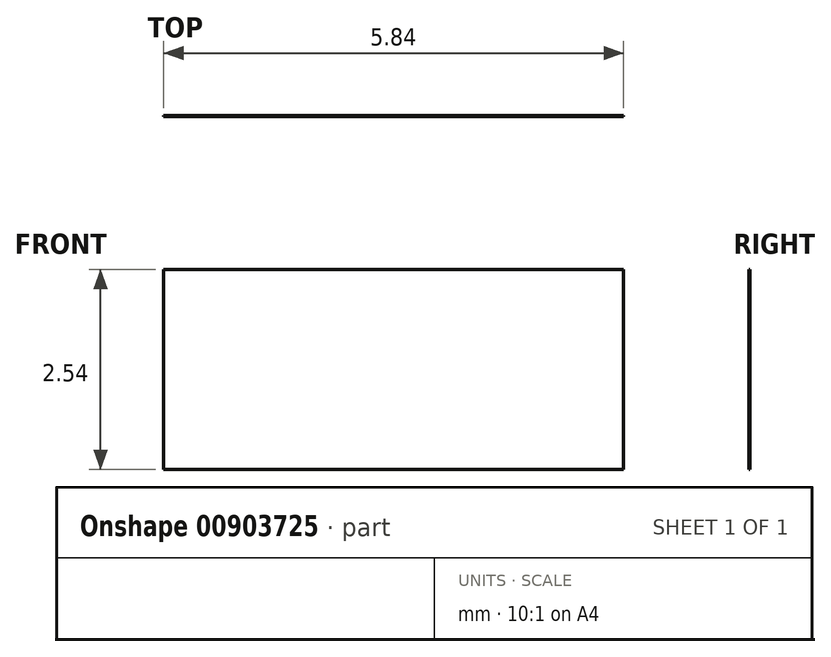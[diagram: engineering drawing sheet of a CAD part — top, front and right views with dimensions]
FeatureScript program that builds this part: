
annotation { "Feature Type Name" : "Feature", "Feature Type Description" : "" }
export const myFeature = defineFeature(function(context is Context, id is Id, definition is map)
    precondition{}
    {
        {
            var Q0;
            Q0=qCreatedBy(makeId("Front.planeOp"),FACE);
            var sketch = newSketch(context, id + "F0", { "sketchPlane" : qUnion([Q0])});
            skLineSegment(sketch, "E0", {"start": v(0, 0) * mm, "end": v(0, 12.7) * mm});
            skLineSegment(sketch, "E1", {"start": v(0, 12.7) * mm, "end": v(10.16, 12.7) * mm});
            skLineSegment(sketch, "E2", {"start": v(10.16, 12.7) * mm, "end": v(10.16, 10.16) * mm});
            skLineSegment(sketch, "E3", {"start": v(10.16, 10.16) * mm, "end": v(56.13, 10.16) * mm});
            skLineSegment(sketch, "E4", {"start": v(56.13, 10.16) * mm, "end": v(56.13, 12.7) * mm});
            skLineSegment(sketch, "E5", {"start": v(56.13, 12.7) * mm, "end": v(66.3, 12.7) * mm});
            skLineSegment(sketch, "E6", {"start": v(66.3, 12.7) * mm, "end": v(66.3, 0) * mm});
            skLineSegment(sketch, "E7", {"start": v(66.3, 0) * mm, "end": v(0, 0) * mm});
            skLineSegment(sketch, "E8", {"start": v(5.84, 15.24) * mm, "end": v(-0.5, 15.24) * mm});
            skLineSegment(sketch, "E9", {"start": v(-0.5, 15.24) * mm, "end": v(-10.88, 3.85) * mm});
            skLineSegment(sketch, "E10", {"start": v(0, 0) * mm, "end": v(-6.65, 0) * mm});
            skCircle(sketch, "E11", {"center": v(-6.65, 0) * mm, "radius": 5.72 * mm});
            skCircle(sketch, "E12", {"center": v(-6.65, 0) * mm, "radius": 3.18 * mm});
            skLineSegment(sketch, "E13", {"start": v(5.84, 15.24) * mm, "end": v(5.84, -9.4) * mm});
            skLineSegment(sketch, "E14", {"start": v(5.84, -9.4) * mm, "end": v(-8.18, -5.5) * mm});
            skSolve(sketch);
        }
        {
            var Q0;
            {var subQ0=sQuery(id+"F0.wireOp",EDGE,"E2");Q0=makeQuery(id+"F0.imprint","IMPRINT",FACE,{"disambiguationData":[TD([[makeQuery(id+"F0.imprint","IMPRINT",EDGE,{"derivedFrom":subQ0}),-1.0]])]});}
            var Q1;
            {var subQ0=sQuery(id+"F0.wireOp",EDGE,"E0");Q1=makeQuery(id+"F0.imprint","IMPRINT",FACE,{"disambiguationData":[TD([[makeQuery(id+"F0.imprint","IMPRINT",EDGE,{"derivedFrom":subQ0}),-1.0]])]});}
            var Q2;
            Q2=sQuery(id+"F0.wireOp",EDGE,"E7");
            revolve(context, id + "F1", {"surfaceOperationType" : NewSurfaceOperationType.NEW, "entities" : qUnion([Q0, Q1]), "axis" : qUnion([Q2]), "revolveType" : RevolveType.FULL});
        }
        {
            var Q0;
            {var subQ1=sQuery(id+"F0.wireOp",EDGE,"E0");Q0=makeQuery(id+"F0.imprint","IMPRINT",FACE,{"disambiguationData":[TD([[makeQuery(id+"F0.imprint","IMPRINT",EDGE,{"derivedFrom":subQ1}),1.0]])]});}
            var Q1;
            {var subQ5=sQuery(id+"F0.wireOp",EDGE,"E12");Q1=makeQuery(id+"F0.imprint","IMPRINT",FACE,{"disambiguationData":[TD([[makeQuery(id+"F0.imprint","IMPRINT",EDGE,{"derivedFrom":subQ5}),-1.0]])]});}
            var Q2;
            {var subQ0=sQuery(id+"F0.wireOp",EDGE,"E14");Q2=makeQuery(id+"F0.imprint","IMPRINT",FACE,{"disambiguationData":[TD([[makeQuery(id+"F0.imprint","IMPRINT",EDGE,{"derivedFrom":subQ0}),-1.0]])]});}
            var Q3;
            Q3=sQuery(id+"F0.wireOp",EDGE,"E13");
            var Q4;
            Q4=sQuery(id+"F0.wireOp",EDGE,"E8");
            var Q5;
            Q5=sQuery(id+"F0.wireOp",EDGE,"E9");
            var Q6;
            Q6=sQuery(id+"F0.wireOp",EDGE,"E11");
            var Q7;
            Q7=sQuery(id+"F0.wireOp",EDGE,"E14");
            var Q8;
            Q8=sQuery(id+"F0.wireOp",EDGE,"E12");
            extrude(context, id + "F2", {"entities" : qUnion([Q0, Q1, Q2]), "surfaceEntities" : qUnion([Q3, Q4, Q5, Q6, Q7, Q8]), "oppositeDirection" : true, "depth" : 1 / 203.2 * mm, "offsetDistance" : 25.4 * mm, "hasSecondDirection" : true, "secondDirectionOppositeDirection" : false, "secondDirectionDepth" : 1 / 203.2 * mm});
        }
        {
            var Q0;
            Q0=makeQuery(id+"F1.opRevolve","SWEPT_FACE",FACE,{"disambiguationData":[OSD([sQuery(id+"F0.wireOp",EDGE,"E6")])]});
            var sketch = newSketch(context, id + "F3", { "sketchPlane" : qUnion([Q0])});
            skCircle(sketch, "E15", {"center": v(0, 0) * mm, "radius": 5.08 * mm});
            skCircle(sketch, "E16", {"center": v(0, 0) * mm, "radius": 1.52 * mm});
            skLineSegment(sketch, "E17", {"start": v(-4.77, -1.75) * mm, "end": v(-4.9, -1.37) * mm});
            skLineSegment(sketch, "E18", {"start": v(5.08, 0) * mm, "end": v(5.08, 15.24) * mm});
            skLineSegment(sketch, "E19", {"start": v(5.08, 15.24) * mm, "end": v(-5.08, 15.24) * mm});
            skLineSegment(sketch, "E20", {"start": v(-5.08, 15.24) * mm, "end": v(-5.08, 0) * mm});
            skSolve(sketch);
        }
        {
            var Q0;
            Q0 = qSketchRegion(id + "F3", true);
            var Q1;
            Q1 = qSketchRegion(id + "F5", true);
            extrude(context, id + "F4", {"entities" : qUnion([Q0, Q1]), "operationType" : NewBodyOperationType.ADD, "oppositeDirection" : true, "depth" : 1.27 * mm, "offsetDistance" : 25.4 * mm, "hasSecondDirection" : true, "secondDirectionOppositeDirection" : false, "secondDirectionDepth" : 6.35 * mm});
        }
        {
            var Q0;
            Q0=makeQuery(id+"F4.opExtrude","SWEPT_FACE",FACE,{"disambiguationData":[OSD([sQuery(id+"F3.wireOp",EDGE,"E20")])]});
            var sketch = newSketch(context, id + "F5", { "sketchPlane" : qUnion([Q0])});
            skLineSegment(sketch, "E21", {"start": v(65.02, 15.24) * mm, "end": v(72.64, 15.24) * mm});
            skLineSegment(sketch, "E22", {"start": v(72.64, 15.24) * mm, "end": v(76.74, 15.24) * mm});
            skSolve(sketch);
        }
        {
            var Q0;
            Q0=makeQuery(id+"F4.opExtrude","SWEPT_FACE",FACE,{"disambiguationData":[OSD([sQuery(id+"F3.wireOp",EDGE,"E19")])]});
            var sketch = newSketch(context, id + "F6", { "sketchPlane" : qUnion([Q0])});
            skLineSegment(sketch, "E23", {"start": v(65.02, -5.08) * mm, "end": v(72.64, 5.08) * mm});
            skLineSegment(sketch, "E24", {"start": v(72.64, -5.08) * mm, "end": v(65.02, 5.08) * mm});
            skCircle(sketch, "E25", {"center": v(68.83, 0) * mm, "radius": 1.52 * mm});
            skSolve(sketch);
        }
        {
            var Q0;
            {var subQ0=sQuery(id+"F6.wireOp",EDGE,"E25");var subQ1=sQuery(id+"F6.wireOp",EDGE,"E23");var subQ2=makeQuery(id+"F6.imprint","INTERSECT",VERTEX,{"disambiguationData":[OD(0.0)],"derivedFrom":[subQ1,subQ0]});Q0=makeQuery(id+"F6.imprint","IMPRINT",FACE,{"disambiguationData":[TD([[makeQuery(id+"F6.imprint","IMPRINT",EDGE,{"disambiguationData":[TD([[subQ2,-1.0]])],"derivedFrom":subQ1}),1.0]])]});}
            var Q1;
            {var subQ0=sQuery(id+"F6.wireOp",EDGE,"E24");var subQ1=sQuery(id+"F6.wireOp",EDGE,"E23");var subQ2=makeQuery(id+"F6.imprint","INTERSECT",VERTEX,{"derivedFrom":[subQ1,subQ0]});Q1=makeQuery(id+"F6.imprint","IMPRINT",FACE,{"disambiguationData":[TD([[makeQuery(id+"F6.imprint","IMPRINT",EDGE,{"disambiguationData":[TD([[subQ2,-1.0]])],"derivedFrom":subQ1}),1.0]])]});}
            var Q2;
            {var subQ0=sQuery(id+"F6.wireOp",EDGE,"E24");var subQ1=sQuery(id+"F6.wireOp",EDGE,"E23");var subQ2=makeQuery(id+"F6.imprint","INTERSECT",VERTEX,{"derivedFrom":[subQ1,subQ0]});Q2=makeQuery(id+"F6.imprint","IMPRINT",FACE,{"disambiguationData":[TD([[makeQuery(id+"F6.imprint","IMPRINT",EDGE,{"disambiguationData":[TD([[subQ2,-1.0]])],"derivedFrom":subQ1}),-1.0]])]});}
            var Q3;
            {var subQ0=sQuery(id+"F6.wireOp",EDGE,"E25");var subQ1=sQuery(id+"F6.wireOp",EDGE,"E23");var subQ2=makeQuery(id+"F6.imprint","INTERSECT",VERTEX,{"disambiguationData":[OD(0.0)],"derivedFrom":[subQ1,subQ0]});Q3=makeQuery(id+"F6.imprint","IMPRINT",FACE,{"disambiguationData":[TD([[makeQuery(id+"F6.imprint","IMPRINT",EDGE,{"disambiguationData":[TD([[subQ2,-1.0]])],"derivedFrom":subQ1}),-1.0]])]});}
            extrude(context, id + "F7", {"entities" : qUnion([Q0, Q1, Q2, Q3]), "operationType" : NewBodyOperationType.ADD, "oppositeDirection" : true, "depth" : 10.4 * mm, "offsetDistance" : 25.4 * mm});
        }
        {
            var Q0;
            Q0=makeQuery(id+"F2.opExtrude","SWEPT_FACE",FACE,{"disambiguationData":[OSD([sQuery(id+"F0.wireOp",EDGE,"E1")])]});
            extrude(context, id + "F8", {"entities" : qUnion([Q0]), "operationType" : NewBodyOperationType.INTERSECT, "oppositeDirection" : true, "depth" : 25.4 * mm, "offsetDistance" : 25.4 * mm});
        }
    });
